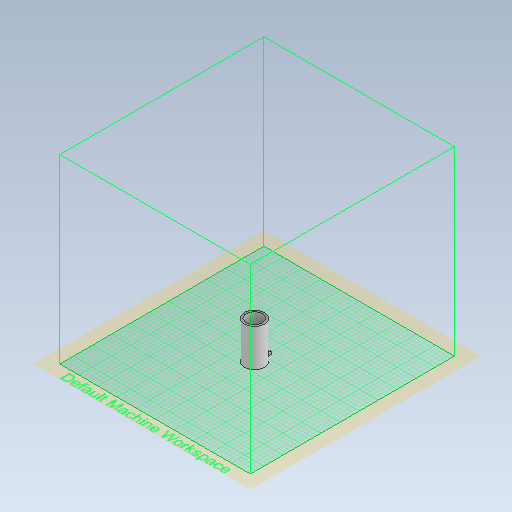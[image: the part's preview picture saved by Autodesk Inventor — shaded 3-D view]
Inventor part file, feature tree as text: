
AUTODESK INVENTOR PART (.ipt)
format: ipt  version: 2021 (Build 250183000, 183)  size: 545,280 bytes
history: native  units: in
note: dims shown in document units (in); Inventor stores cm internally (conversion verified against a paired STEP export)
features: projected_geometry x10, extrude x8, sketch x6, fillet x2, plane x1, chamfer x1
ambient origin geometry x8: Origin, YZ Plane, XZ Plane, XY Plane, X Axis, Y Axis, Z Axis, Center Point
bodies: Solid1 (feature_tree)
feature tree (28):
  extrude  "Extrusion1"  Depth=3.2677in TaperAngle=0.0deg
  plane  "Work Plane1"
  extrude  "Extrusion7"  Depth=3.189in TaperAngle=0.0deg
  extrude  "Extrusion8"  Depth=0.3937in
  extrude  "Extrusion9"  Depth=0.3937in
  extrude  "Extrusion10"  Depth=0.0295in TaperAngle=0.0deg
  extrude  "Extrusion11"  Depth=0.3937in
  extrude  "Extrusion13"  Depth=0.3937in TaperAngle=0.0deg
  chamfer  "Chamfer4"  Distance=1.1811in
  extrude  "Extrusion14"  Depth=0.3937in
  fillet  "Fillet11"  Radius=0.3937in
  fillet  "Fillet12"  Radius=0.0059in
  sketch  "Sketch2"  dims[d2=1.752in d3=3.2677in d4=0.0in]
  sketch  "Sketch9"  dims[d54=1.4173in d55=3.189in d56=0.0in]
  projected_geometry  "Projected Loop7"
  sketch  "Sketch10"  dims[d57=0.3937in d58=0.2756in]
  projected_geometry  "Projected Loop8"
  sketch  "Sketch11"  dims[d59=0.3937in d60=0.0236in d61=0.0in d62=0.0in d63=0.1693in]
  projected_geometry  "Projected Loop9"
  projected_geometry  "Projected Loop10"
  projected_geometry  "Projected Loop11"
  projected_geometry  "Projected Loop12"
  projected_geometry  "Projected Loop14"
  sketch  "Sketch16"  dims[d64=0.1024in d66=0.0295in d67=0.0in]
  projected_geometry  "Projected Loop16"
  sketch  "Sketch17"  dims[d68=0.0591in d69=0.0591in d71=0.1969in d72=0.0in d76=1.1811in d77=0.0in d92=0.1181in d93=0.3937in d94=0.0in d96=0.0059in d103=0.1575in d104=0.0787in d105=45.0deg d109=0.2756in d110=0.0787in d111=0.0in d116=0.4724in d117=0.3937in d121=0.0984in d19=0.0197in d20=0.0344in d21=0.0197in d22=0.0344in]
  projected_geometry  "Projected Loop17"
  projected_geometry  "Projected Loop18"
